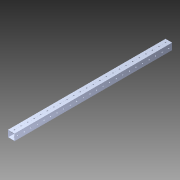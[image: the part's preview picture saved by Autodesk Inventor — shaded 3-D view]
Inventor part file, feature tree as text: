
AUTODESK INVENTOR PART (.ipt)
format: ipt  version: 2014 SP1 (Build 180222100, 222)  size: 1,544,192 bytes
history: native  units: in
note: dims shown in document units (in); Inventor stores cm internally (conversion verified against a paired STEP export)
features: extrude x2, sketch x2, pattern_circular x1, other x1, mirror x1, imported_body x1
ambient origin geometry x8: Origin, YZ Plane, XZ Plane, XY Plane, X Axis, Y Axis, Z Axis, Center Point
bodies: Body1 (feature_tree)
feature tree (8):
  pattern_circular  "CirPattern2"
  other  "1x1 tube1"
  extrude  "Extrusion1"  Depth=18.0in TaperAngle=0.0deg
  mirror  "Mirror1"
  extrude  "Extrusion2"  [1 undecoded]
  imported_body  "Base1"
  sketch  "Sketch1"  dims[d0=38.0in d1=0.0in d2=18.0in d3=0.0in]
  sketch  "Sketch3"
note: 1 required parameter value undecoded (feature->parameter linkage not recoverable at this tier; creation-order binding heuristic only, values carry confidence <= 0.55)
